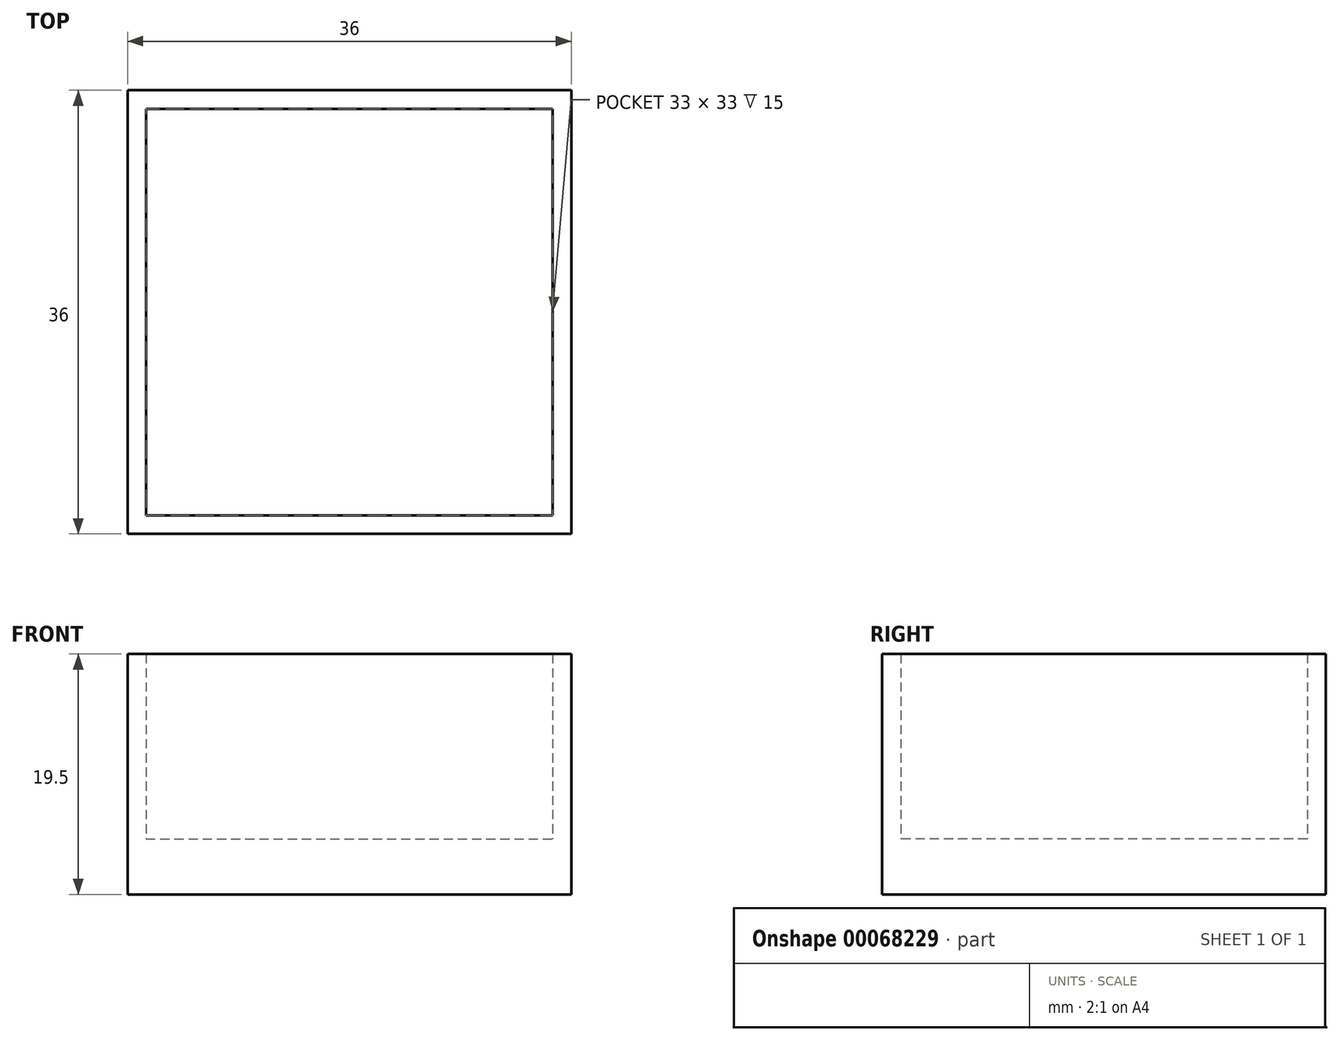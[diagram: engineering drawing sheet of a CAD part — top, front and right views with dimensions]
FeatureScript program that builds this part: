
annotation { "Feature Type Name" : "Feature", "Feature Type Description" : "" }
export const myFeature = defineFeature(function(context is Context, id is Id, definition is map)
    precondition{}
    {
        {
            var Q0;
            Q0=qCreatedBy(makeId("Top.planeOp"),FACE);
            var sketch = newSketch(context, id + "F0", { "sketchPlane" : qUnion([Q0])});
            skLineSegment(sketch, "E0.bottom", {"start": v(-16.5, 16.5) * mm, "end": v(16.5, 16.5) * mm});
            skLineSegment(sketch, "E0.top", {"start": v(-16.5, -16.5) * mm, "end": v(16.5, -16.5) * mm});
            skLineSegment(sketch, "E0.left", {"start": v(-16.5, 16.5) * mm, "end": v(-16.5, -16.5) * mm});
            skLineSegment(sketch, "E0.right", {"start": v(16.5, 16.5) * mm, "end": v(16.5, -16.5) * mm});
            skPoint(sketch, "E0.middle", {"position": v(0, 0) * mm});
            skSolve(sketch);
        }
        {
            var Q0;
            Q0 = qSketchRegion(id + "F0", true);
            extrude(context, id + "F1", {"entities" : qUnion([Q0]), "depth" : 15 * mm});
        }
        {
            var Q0;
            Q0=makeQuery(id+"F1.opExtrude","CAP_FACE",FACE,{"disambiguationData":[OSD([sQuery(id+"F0.wireOp",EDGE,"E0.bottom"),sQuery(id+"F0.wireOp",EDGE,"E0.top"),sQuery(id+"F0.wireOp",EDGE,"E0.left"),sQuery(id+"F0.wireOp",EDGE,"E0.right")])],"isStart":false});
            shell(context, id + "F2", {"entities" : qUnion([Q0]), "thickness" : 1.5 * mm, "oppositeDirection" : true});
        }
        {
            var Q0;
            Q0=makeQuery(id+"F1.opExtrude","CAP_FACE",FACE,{"disambiguationData":[OSD([sQuery(id+"F0.wireOp",EDGE,"E0.bottom"),sQuery(id+"F0.wireOp",EDGE,"E0.top"),sQuery(id+"F0.wireOp",EDGE,"E0.left"),sQuery(id+"F0.wireOp",EDGE,"E0.right")])],"isStart":true});
            extrude(context, id + "F3", {"entities" : qUnion([Q0]), "operationType" : NewBodyOperationType.ADD, "depth" : 3 * mm});
        }
    });
